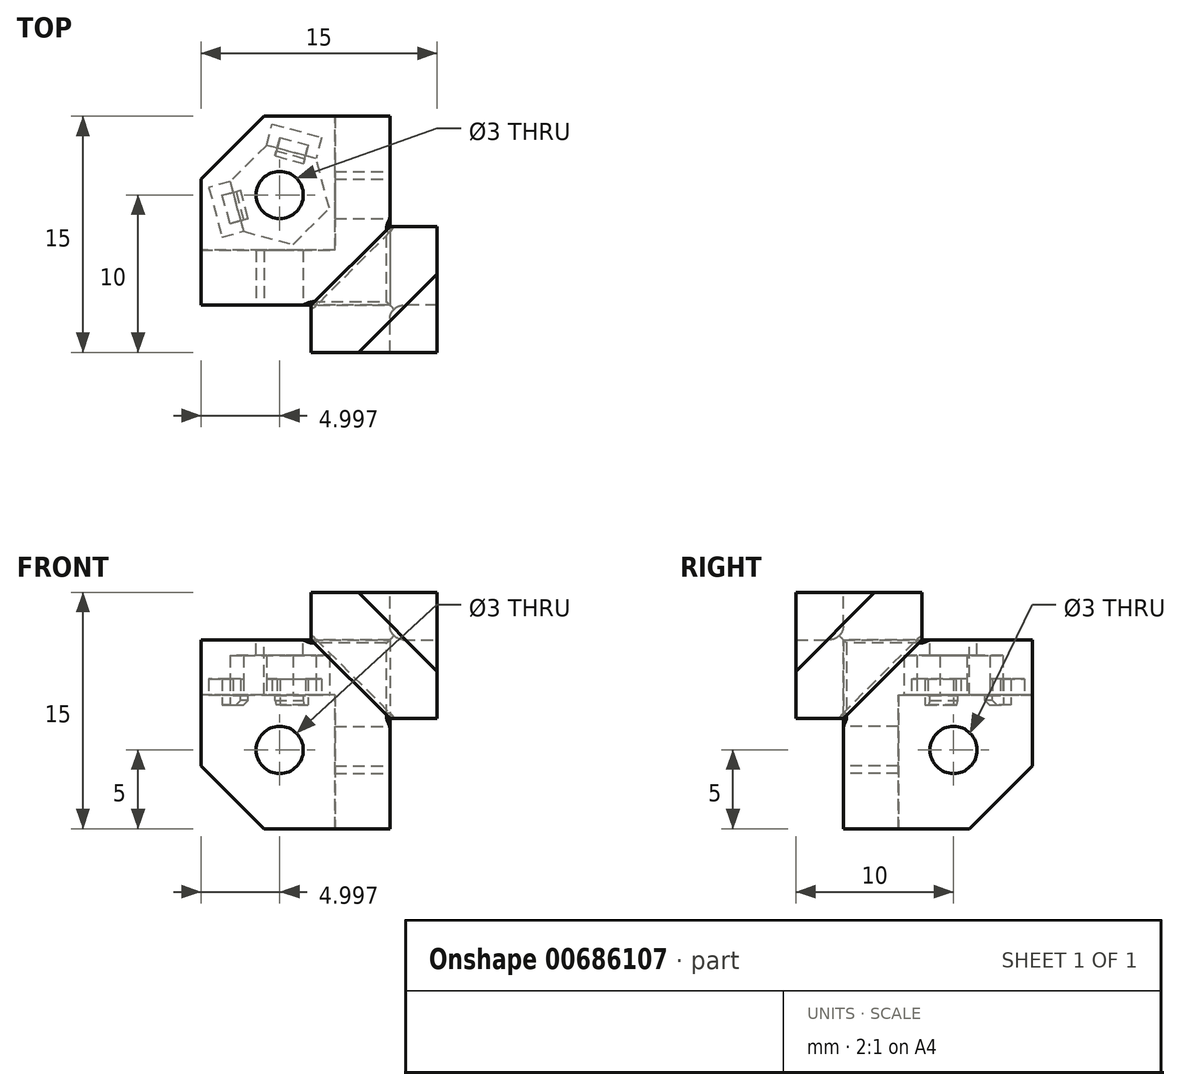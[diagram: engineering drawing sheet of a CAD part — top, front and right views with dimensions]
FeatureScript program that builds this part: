
annotation { "Feature Type Name" : "Feature", "Feature Type Description" : "" }
export const myFeature = defineFeature(function(context is Context, id is Id, definition is map)
    precondition{}
    {
        {
            var Q0;
            Q0=qCreatedBy(makeId("Front.planeOp"),FACE);
            var sketch = newSketch(context, id + "F0", { "sketchPlane" : qUnion([Q0])});
            skLineSegment(sketch, "E0", {"start": v(7.23, 37.22) * mm, "end": v(15.23, 37.22) * mm});
            skLineSegment(sketch, "E1", {"start": v(15.23, 37.22) * mm, "end": v(15.23, 29.22) * mm});
            skLineSegment(sketch, "E2", {"start": v(15.23, 29.22) * mm, "end": v(12.23, 29.22) * mm});
            skLineSegment(sketch, "E3", {"start": v(12.23, 29.22) * mm, "end": v(7.23, 34.22) * mm});
            skLineSegment(sketch, "E4", {"start": v(7.23, 34.22) * mm, "end": v(7.23, 37.22) * mm});
            skLineSegment(sketch, "E5", {"start": v(15.23, 29.22) * mm, "end": v(15.23, 27.22) * mm, "construction": true});
            skLineSegment(sketch, "E6", {"start": v(15.23, 27.22) * mm, "end": v(5.23, 27.22) * mm, "construction": true});
            skCircle(sketch, "E7", {"center": v(5.23, 27.22) * mm, "radius": 1.5 * mm});
            skLineSegment(sketch, "E8", {"start": v(7.23, 37.22) * mm, "end": v(0.23, 37.22) * mm});
            skLineSegment(sketch, "E9", {"start": v(0.23, 37.22) * mm, "end": v(0.23, 26.22) * mm});
            skLineSegment(sketch, "E10", {"start": v(0.23, 26.22) * mm, "end": v(4.23, 22.22) * mm});
            skLineSegment(sketch, "E11", {"start": v(4.23, 22.22) * mm, "end": v(15.23, 22.22) * mm});
            skLineSegment(sketch, "E12", {"start": v(15.23, 22.22) * mm, "end": v(15.23, 29.22) * mm});
            skSolve(sketch);
        }
        {
            var Q0;
            Q0=makeQuery(id+"F0.imprint","IMPRINT",FACE,{"disambiguationData":[TD([[makeQuery(id+"F0.imprint","IMPRINT",EDGE,{"derivedFrom":sQuery(id+"F0.wireOp",EDGE,"E0")}),-1.0]])]});
            extrude(context, id + "F1", {"entities" : qUnion([Q0]), "depth" : 3 * mm, "offsetDistance" : 25 * mm});
        }
        {
            var Q0;
            Q0=makeQuery(id+"F0.imprint","IMPRINT",FACE,{"disambiguationData":[TD([[makeQuery(id+"F0.imprint","IMPRINT",EDGE,{"derivedFrom":sQuery(id+"F0.wireOp",EDGE,"E2")}),1.0]])]});
            var Q1;
            Q1=makeQuery(id+"F0.imprint","IMPRINT",FACE,{"disambiguationData":[TD([[makeQuery(id+"F0.imprint","IMPRINT",EDGE,{"derivedFrom":sQuery(id+"F0.wireOp",EDGE,"E0")}),-1.0]])]});
            extrude(context, id + "F2", {"entities" : qUnion([Q0, Q1]), "operationType" : NewBodyOperationType.ADD, "oppositeDirection" : true, "depth" : 2.5 * mm, "offsetDistance" : 25 * mm});
        }
        {
            var Q0;
            {var subQ0=sQuery(id+"F0.wireOp",EDGE,"E0");Q0=makeQuery(id+"F2.boolean.opBoolean","MERGE",FACE,{"derivedFrom":[makeQuery(id+"F1.opExtrude","SWEPT_FACE",FACE,{"disambiguationData":[OSD([subQ0])]}),makeQuery(id+"F2.opExtrude","SWEPT_FACE",FACE,{"disambiguationData":[OSD([subQ0,sQuery(id+"F0.wireOp",EDGE,"E8")])]})]});}
            var sketch = newSketch(context, id + "F3", { "sketchPlane" : qUnion([Q0])});
            skLineSegment(sketch, "E13", {"start": v(7.23, -3) * mm, "end": v(15.23, -3) * mm});
            skLineSegment(sketch, "E14", {"start": v(15.23, -3) * mm, "end": v(15.23, 5) * mm});
            skLineSegment(sketch, "E15", {"start": v(15.23, 5) * mm, "end": v(12.23, 5) * mm});
            skLineSegment(sketch, "E16", {"start": v(12.23, 5) * mm, "end": v(7.23, 0) * mm});
            skLineSegment(sketch, "E17", {"start": v(12.23, 5) * mm, "end": v(12.23, 12) * mm});
            skLineSegment(sketch, "E18", {"start": v(12.23, 12) * mm, "end": v(4.23, 12) * mm});
            skLineSegment(sketch, "E19", {"start": v(4.23, 12) * mm, "end": v(0.23, 8) * mm});
            skPoint(sketch, "E19.endSnap0", {"position": v(0.23, 1.25) * mm});
            skLineSegment(sketch, "E20", {"start": v(0.23, 8) * mm, "end": v(0.23, 0) * mm});
            skLineSegment(sketch, "E21", {"start": v(8.02, -3) * mm, "end": v(5.23, -3) * mm, "construction": true});
            skLineSegment(sketch, "E22", {"start": v(5.23, -3) * mm, "end": v(5.23, 7) * mm, "construction": true});
            skCircle(sketch, "E23", {"center": v(5.23, 7) * mm, "radius": 1.5 * mm});
            skSolve(sketch);
        }
        {
            var Q0;
            {var subQ1=sQuery(id+"F3.wireOp",EDGE,"E17");Q0=makeQuery(id+"F3.imprint","IMPRINT",FACE,{"disambiguationData":[TD([[makeQuery(id+"F3.imprint","IMPRINT",EDGE,{"derivedFrom":subQ1}),1.0]])]});}
            var Q1;
            {var subQ3=sQuery(id+"F3.wireOp",EDGE,"E15");Q1=makeQuery(id+"F3.imprint","IMPRINT",FACE,{"disambiguationData":[TD([[makeQuery(id+"F3.imprint","IMPRINT",EDGE,{"derivedFrom":subQ3}),1.0]])]});}
            extrude(context, id + "F4", {"entities" : qUnion([Q0, Q1]), "operationType" : NewBodyOperationType.ADD, "oppositeDirection" : true, "depth" : 5.5 * mm, "offsetDistance" : 25 * mm});
        }
        {
            var Q0;
            {var subQ1=sQuery(id+"F3.wireOp",EDGE,"E17");Q0=makeQuery(id+"F3.imprint","IMPRINT",FACE,{"disambiguationData":[TD([[makeQuery(id+"F3.imprint","IMPRINT",EDGE,{"derivedFrom":subQ1}),1.0]])]});}
            var Q1;
            {var subQ1=sQuery(id+"F0.wireOp",EDGE,"E8");var subQ2=sQuery(id+"F0.wireOp",EDGE,"E0");var subQ3=makeQuery(id+"F2.opExtrude","CAP_EDGE",EDGE,{"disambiguationData":[OSD([subQ2,subQ1])],"isStart":true});Q1=makeQuery(id+"F3.imprint","IMPRINT",FACE,{"disambiguationData":[TD([[makeQuery(id+"F3.imprint","IMPRINT",EDGE,{"derivedFrom":subQ3}),-1.0]])]});}
            extrude(context, id + "F5", {"entities" : qUnion([Q0, Q1]), "operationType" : NewBodyOperationType.REMOVE, "oppositeDirection" : true, "depth" : 3 * mm, "offsetDistance" : 25 * mm});
        }
        {
            var Q0;
            {var subQ0=sQuery(id+"F0.wireOp",EDGE,"E1");Q0=makeQuery(id+"F2.boolean.opBoolean","MERGE",FACE,{"derivedFrom":[makeQuery(id+"F1.opExtrude","SWEPT_FACE",FACE,{"disambiguationData":[OSD([subQ0])]}),makeQuery(id+"F2.opExtrude","SWEPT_FACE",FACE,{"disambiguationData":[OSD([subQ0,sQuery(id+"F0.wireOp",EDGE,"E12")])]})]});}
            var sketch = newSketch(context, id + "F6", { "sketchPlane" : qUnion([Q0])});
            skLineSegment(sketch, "E24", {"start": v(0, 29.22) * mm, "end": v(0, 22.22) * mm});
            skLineSegment(sketch, "E25", {"start": v(0, 22.22) * mm, "end": v(8, 22.22) * mm});
            skLineSegment(sketch, "E26", {"start": v(12, 34.22) * mm, "end": v(12, 26.22) * mm});
            skLineSegment(sketch, "E27", {"start": v(12, 26.22) * mm, "end": v(8, 22.22) * mm});
            skLineSegment(sketch, "E28", {"start": v(-3, 29.22) * mm, "end": v(-3, 27.22) * mm, "construction": true});
            skLineSegment(sketch, "E29", {"start": v(-3, 27.22) * mm, "end": v(7, 27.22) * mm, "construction": true});
            skCircle(sketch, "E30", {"center": v(7, 27.22) * mm, "radius": 1.5 * mm});
            skLineSegment(sketch, "E31", {"start": v(12, 34.22) * mm, "end": v(5, 34.22) * mm});
            skLineSegment(sketch, "E32", {"start": v(5, 34.22) * mm, "end": v(0, 29.22) * mm});
            skSolve(sketch);
        }
        {
            var Q0;
            Q0=qSketchRegion(id+"F6",true);
            extrude(context, id + "F7", {"entities" : qUnion([Q0]), "operationType" : NewBodyOperationType.ADD, "oppositeDirection" : true, "depth" : 5.5 * mm, "offsetDistance" : 25 * mm});
        }
        {
            var Q0;
            {var subQ2=sQuery(id+"F6.wireOp",EDGE,"E24");Q0=makeQuery(id+"F6.imprint","IMPRINT",FACE,{"disambiguationData":[TD([[makeQuery(id+"F6.imprint","IMPRINT",EDGE,{"derivedFrom":subQ2}),-1.0]])]});}
            var Q1;
            Q1=makeQuery(id+"F6.imprint","IMPRINT",FACE,{"disambiguationData":[TD([[makeQuery(id+"F6.imprint","IMPRINT",EDGE,{"derivedFrom":sQuery(id+"F6.wireOp",EDGE,"E26")}),-1.0]])]});
            var Q2;
            {var subQ1=sQuery(id+"F3.wireOp",EDGE,"E14");var subQ2=makeQuery(id+"F4.opExtrude","CAP_EDGE",EDGE,{"disambiguationData":[OSD([subQ1])],"isStart":false});Q2=makeQuery(id+"F6.imprint","IMPRINT",FACE,{"disambiguationData":[TD([[makeQuery(id+"F6.imprint","IMPRINT",EDGE,{"derivedFrom":subQ2}),1.0]])]});}
            extrude(context, id + "F8", {"entities" : qUnion([Q0, Q1, Q2]), "operationType" : NewBodyOperationType.REMOVE, "oppositeDirection" : true, "depth" : 3 * mm, "offsetDistance" : 25 * mm});
        }
        {
            var Q0;
            Q0=makeQuery(id+"F1.opExtrude","CAP_FACE",FACE,{"disambiguationData":[OSD([sQuery(id+"F0.wireOp",EDGE,"E0"),sQuery(id+"F0.wireOp",EDGE,"E1"),sQuery(id+"F0.wireOp",EDGE,"E2"),sQuery(id+"F0.wireOp",EDGE,"E3"),sQuery(id+"F0.wireOp",EDGE,"E4")])],"isStart":false});
            var sketch = newSketch(context, id + "F9", { "sketchPlane" : qUnion([Q0])});
            skLineSegment(sketch, "E33", {"start": v(15.23, 37.22) * mm, "end": v(15.23, 32.22) * mm});
            skLineSegment(sketch, "E34", {"start": v(15.23, 32.22) * mm, "end": v(10.23, 37.22) * mm});
            skLineSegment(sketch, "E35", {"start": v(10.23, 37.22) * mm, "end": v(15.23, 37.22) * mm});
            skSolve(sketch);
        }
        {
            var Q0;
            Q0=makeQuery(id+"F9.imprint","IMPRINT",FACE,{"disambiguationData":[TD([[makeQuery(id+"F9.imprint","IMPRINT",EDGE,{"derivedFrom":sQuery(id+"F9.wireOp",EDGE,"E33")}),-1.0]])]});
            extrude(context, id + "F10", {"entities" : qUnion([Q0]), "operationType" : NewBodyOperationType.REMOVE, "oppositeDirection" : true, "depth" : 5 * mm, "offsetDistance" : 25 * mm});
        }
        {
            var Q0;
            Q0=makeQuery(id+"F10.boolean.opBoolean","COPY",EDGE,{"derivedFrom":makeQuery(id+"F10.opExtrude","CAP_EDGE",EDGE,{"disambiguationData":[OSD([sQuery(id+"F9.wireOp",EDGE,"E34")])],"isStart":false})});
            chamfer(context, id + "F11", {"entities" : qUnion([Q0]), "chamferType" : ChamferType.OFFSET_ANGLE, "width" : 5 * mm, "oppositeDirection" : false, "angle" : 35.4 * degree, "tangentPropagation" : true});
        }
        {
            var Q0;
            {var subQ0=sQuery(id+"F0.wireOp",EDGE,"E2");Q0=makeQuery(id+"F8.boolean.opBoolean","MERGE",VERTEX,{"derivedFrom":[makeQuery(id+"F1.opExtrude","CAP_VERTEX",VERTEX,{"disambiguationData":[OSD([subQ0,sQuery(id+"F0.wireOp",EDGE,"E3")])],"isStart":true}),makeQuery(id+"F8.opExtrude","CAP_VERTEX",VERTEX,{"disambiguationData":[OSD([sQuery(id+"F0.wireOp",EDGE,"E1"),subQ0,sQuery(id+"F0.wireOp",EDGE,"E12"),sQuery(id+"F6.wireOp",EDGE,"E24"),sQuery(id+"F6.wireOp",EDGE,"E32")])],"isStart":false})]});}
            var Q1;
            {var subQ0=sQuery(id+"F0.wireOp",EDGE,"E4");Q1=makeQuery(id+"F5.boolean.opBoolean","MERGE",VERTEX,{"derivedFrom":[makeQuery(id+"F1.opExtrude","CAP_VERTEX",VERTEX,{"disambiguationData":[OSD([sQuery(id+"F0.wireOp",EDGE,"E3"),subQ0])],"isStart":true}),makeQuery(id+"F5.opExtrude","CAP_VERTEX",VERTEX,{"disambiguationData":[OSD([sQuery(id+"F0.wireOp",EDGE,"E0"),subQ0,sQuery(id+"F0.wireOp",EDGE,"E8"),sQuery(id+"F3.wireOp",EDGE,"E16")])],"isStart":false})]});}
            var Q2;
            {var subQ0=sQuery(id+"F3.wireOp",EDGE,"E15");Q2=makeQuery(id+"F8.boolean.opBoolean","MERGE",VERTEX,{"derivedFrom":[makeQuery(id+"F5.boolean.opBoolean","COPY",VERTEX,{"derivedFrom":makeQuery(id+"F5.opExtrude","CAP_VERTEX",VERTEX,{"disambiguationData":[OSD([subQ0,sQuery(id+"F3.wireOp",EDGE,"E16"),sQuery(id+"F3.wireOp",EDGE,"E17")])],"isStart":false})}),makeQuery(id+"F8.opExtrude","CAP_VERTEX",VERTEX,{"disambiguationData":[OSD([sQuery(id+"F3.wireOp",EDGE,"E14"),subQ0,sQuery(id+"F6.wireOp",EDGE,"E31"),sQuery(id+"F6.wireOp",EDGE,"E32")])],"isStart":false})]});}
            cPlane(context, id + "F12", {"entities" : qUnion([Q0, Q1, Q2]), "cplaneType" : CPlaneType.THREE_POINT, "offset" : 25 * mm, "width" : 150 * mm, "height" : 150 * mm});
        }
        {
            var Q0;
            Q0=qCreatedBy(id+"F12.planeOp",FACE);
            var sketch = newSketch(context, id + "F13", { "sketchPlane" : qUnion([Q0])});
            skLineSegment(sketch, "E36", {"start": v(-8.07, 24.2) * mm, "end": v(-1.95, 20.66) * mm});
            skLineSegment(sketch, "E37", {"start": v(-1.95, 27.73) * mm, "end": v(-8.07, 24.2) * mm});
            skLineSegment(sketch, "E38", {"start": v(-1.95, 20.66) * mm, "end": v(-1.95, 27.73) * mm});
            skLineSegment(sketch, "E39.0", {"start": v(-2.15, 27.39) * mm, "end": v(-7.67, 24.2) * mm});
            skLineSegment(sketch, "E39.1", {"start": v(-2.15, 21) * mm, "end": v(-2.15, 27.39) * mm});
            skLineSegment(sketch, "E39.2", {"start": v(-7.67, 24.2) * mm, "end": v(-2.15, 21) * mm});
            skLineSegment(sketch, "E40.0", {"start": v(-1.07, 29.26) * mm, "end": v(-9.83, 24.2) * mm});
            skLineSegment(sketch, "E40.1", {"start": v(-1.07, 19.14) * mm, "end": v(-1.07, 29.26) * mm});
            skLineSegment(sketch, "E40.2", {"start": v(-9.83, 24.2) * mm, "end": v(-1.07, 19.14) * mm});
            skSolve(sketch);
        }
        {
            var Q0;
            Q0=qSketchRegion(id+"F13",true);
            var Q1;
            Q1=makeQuery(id+"F13.imprint","IMPRINT",FACE,{"disambiguationData":[TD([[makeQuery(id+"F13.imprint","IMPRINT",EDGE,{"derivedFrom":sQuery(id+"F13.wireOp",EDGE,"E36")}),1.0]])]});
            extrude(context, id + "F14", {"entities" : qUnion([Q0, Q1]), "operationType" : NewBodyOperationType.REMOVE, "endBound" : BoundingType.SYMMETRIC, "depth" : .6 * mm, "offsetDistance" : 25 * mm});
        }
        {
            var Q0;
            Q0=makeQuery(id+"F14.boolean.opBoolean","COPY",EDGE,{"derivedFrom":makeQuery(id+"F14.opExtrude","CAP_EDGE",EDGE,{"disambiguationData":[OSD([sQuery(id+"F13.wireOp",EDGE,"E39.0")])],"isStart":true})});
            var Q1;
            Q1=makeQuery(id+"F14.boolean.opBoolean","COPY",EDGE,{"derivedFrom":makeQuery(id+"F14.opExtrude","CAP_EDGE",EDGE,{"disambiguationData":[OSD([sQuery(id+"F13.wireOp",EDGE,"E39.1")])],"isStart":true})});
            var Q2;
            Q2=makeQuery(id+"F14.boolean.opBoolean","COPY",EDGE,{"derivedFrom":makeQuery(id+"F14.opExtrude","CAP_EDGE",EDGE,{"disambiguationData":[OSD([sQuery(id+"F13.wireOp",EDGE,"E39.0")])],"isStart":false})});
            var Q3;
            Q3=makeQuery(id+"F14.boolean.opBoolean","COPY",EDGE,{"derivedFrom":makeQuery(id+"F14.opExtrude","CAP_EDGE",EDGE,{"disambiguationData":[OSD([sQuery(id+"F13.wireOp",EDGE,"E39.1")])],"isStart":false})});
            var Q4;
            Q4=makeQuery(id+"F14.boolean.opBoolean","COPY",EDGE,{"derivedFrom":makeQuery(id+"F14.opExtrude","CAP_EDGE",EDGE,{"disambiguationData":[OSD([sQuery(id+"F13.wireOp",EDGE,"E39.2")])],"isStart":true})});
            var Q5;
            Q5=makeQuery(id+"F14.boolean.opBoolean","COPY",EDGE,{"derivedFrom":makeQuery(id+"F14.opExtrude","CAP_EDGE",EDGE,{"disambiguationData":[OSD([sQuery(id+"F13.wireOp",EDGE,"E39.2")])],"isStart":false})});
            fillet(context, id + "F15", {"entities" : qUnion([Q0, Q1, Q2, Q3, Q4, Q5]), "radius" : .3 * mm, "tangentPropagation" : true, "allowEdgeOverflow" : false});
        }
        {
            var Q0;
            Q0=makeQuery(id+"F14.boolean.opBoolean","INTERSECT",EDGE,{"derivedFrom":[makeQuery(id+"F8.boolean.opBoolean","COPY",FACE,{"derivedFrom":makeQuery(id+"F8.opExtrude","SWEPT_FACE",FACE,{"disambiguationData":[OSD([sQuery(id+"F6.wireOp",EDGE,"E32")])]})}),makeQuery(id+"F14.opExtrude","CAP_FACE",FACE,{"disambiguationData":[OSD([sQuery(id+"F13.wireOp",EDGE,"E39.0"),sQuery(id+"F13.wireOp",EDGE,"E39.1"),sQuery(id+"F13.wireOp",EDGE,"E39.2"),sQuery(id+"F13.wireOp",EDGE,"E40.0"),sQuery(id+"F13.wireOp",EDGE,"E40.1"),sQuery(id+"F13.wireOp",EDGE,"E40.2")])],"isStart":false})]});
            var Q1;
            Q1=makeQuery(id+"F14.boolean.opBoolean","INTERSECT",EDGE,{"derivedFrom":[makeQuery(id+"F1.opExtrude","SWEPT_FACE",FACE,{"disambiguationData":[OSD([sQuery(id+"F0.wireOp",EDGE,"E3")])]}),makeQuery(id+"F14.opExtrude","CAP_FACE",FACE,{"disambiguationData":[OSD([sQuery(id+"F13.wireOp",EDGE,"E39.0"),sQuery(id+"F13.wireOp",EDGE,"E39.1"),sQuery(id+"F13.wireOp",EDGE,"E39.2"),sQuery(id+"F13.wireOp",EDGE,"E40.0"),sQuery(id+"F13.wireOp",EDGE,"E40.1"),sQuery(id+"F13.wireOp",EDGE,"E40.2")])],"isStart":false})]});
            var Q2;
            Q2=makeQuery(id+"F14.boolean.opBoolean","INTERSECT",EDGE,{"derivedFrom":[makeQuery(id+"F5.boolean.opBoolean","COPY",FACE,{"derivedFrom":makeQuery(id+"F5.opExtrude","SWEPT_FACE",FACE,{"disambiguationData":[OSD([sQuery(id+"F3.wireOp",EDGE,"E16")])]})}),makeQuery(id+"F14.opExtrude","CAP_FACE",FACE,{"disambiguationData":[OSD([sQuery(id+"F13.wireOp",EDGE,"E39.0"),sQuery(id+"F13.wireOp",EDGE,"E39.1"),sQuery(id+"F13.wireOp",EDGE,"E39.2"),sQuery(id+"F13.wireOp",EDGE,"E40.0"),sQuery(id+"F13.wireOp",EDGE,"E40.1"),sQuery(id+"F13.wireOp",EDGE,"E40.2")])],"isStart":false})]});
            fillet(context, id + "F16", {"entities" : qUnion([Q0, Q1, Q2]), "radius" : 1 * mm, "tangentPropagation" : true, "allowEdgeOverflow" : false});
        }
        {
            var Q0;
            Q0=makeQuery(id+"F14.boolean.opBoolean","INTERSECT",EDGE,{"derivedFrom":[makeQuery(id+"F2.opExtrude","CAP_FACE",FACE,{"disambiguationData":[OSD([sQuery(id+"F0.wireOp",EDGE,"E0"),sQuery(id+"F0.wireOp",EDGE,"E1"),sQuery(id+"F0.wireOp",EDGE,"E7"),sQuery(id+"F0.wireOp",EDGE,"E8"),sQuery(id+"F0.wireOp",EDGE,"E9"),sQuery(id+"F0.wireOp",EDGE,"E10"),sQuery(id+"F0.wireOp",EDGE,"E11"),sQuery(id+"F0.wireOp",EDGE,"E12")])],"isStart":true}),makeQuery(id+"F14.opExtrude","CAP_FACE",FACE,{"disambiguationData":[OSD([sQuery(id+"F13.wireOp",EDGE,"E39.0"),sQuery(id+"F13.wireOp",EDGE,"E39.1"),sQuery(id+"F13.wireOp",EDGE,"E39.2"),sQuery(id+"F13.wireOp",EDGE,"E40.0"),sQuery(id+"F13.wireOp",EDGE,"E40.1"),sQuery(id+"F13.wireOp",EDGE,"E40.2")])],"isStart":true})]});
            var Q1;
            Q1=makeQuery(id+"F14.boolean.opBoolean","INTERSECT",EDGE,{"derivedFrom":[makeQuery(id+"F8.boolean.opBoolean","COPY",FACE,{"derivedFrom":makeQuery(id+"F8.opExtrude","CAP_FACE",FACE,{"disambiguationData":[OSD([sQuery(id+"F6.wireOp",EDGE,"E24"),sQuery(id+"F6.wireOp",EDGE,"E25"),sQuery(id+"F6.wireOp",EDGE,"E26"),sQuery(id+"F6.wireOp",EDGE,"E27"),sQuery(id+"F6.wireOp",EDGE,"E30"),sQuery(id+"F6.wireOp",EDGE,"E31"),sQuery(id+"F6.wireOp",EDGE,"E32")])],"isStart":false})}),makeQuery(id+"F14.opExtrude","CAP_FACE",FACE,{"disambiguationData":[OSD([sQuery(id+"F13.wireOp",EDGE,"E39.0"),sQuery(id+"F13.wireOp",EDGE,"E39.1"),sQuery(id+"F13.wireOp",EDGE,"E39.2"),sQuery(id+"F13.wireOp",EDGE,"E40.0"),sQuery(id+"F13.wireOp",EDGE,"E40.1"),sQuery(id+"F13.wireOp",EDGE,"E40.2")])],"isStart":true})]});
            var Q2;
            Q2=makeQuery(id+"F14.boolean.opBoolean","INTERSECT",EDGE,{"derivedFrom":[makeQuery(id+"F7.boolean.opBoolean","MERGE",FACE,{"derivedFrom":[makeQuery(id+"F5.boolean.opBoolean","COPY",FACE,{"derivedFrom":makeQuery(id+"F5.opExtrude","CAP_FACE",FACE,{"disambiguationData":[OSD([sQuery(id+"F0.wireOp",EDGE,"E0"),sQuery(id+"F0.wireOp",EDGE,"E8"),sQuery(id+"F3.wireOp",EDGE,"E16"),sQuery(id+"F3.wireOp",EDGE,"E17"),sQuery(id+"F3.wireOp",EDGE,"E18"),sQuery(id+"F3.wireOp",EDGE,"E19"),sQuery(id+"F3.wireOp",EDGE,"E20"),sQuery(id+"F3.wireOp",EDGE,"E23")])],"isStart":false})}),makeQuery(id+"F7.opExtrude","SWEPT_FACE",FACE,{"disambiguationData":[OSD([sQuery(id+"F6.wireOp",EDGE,"E31")])]})]}),makeQuery(id+"F14.opExtrude","CAP_FACE",FACE,{"disambiguationData":[OSD([sQuery(id+"F13.wireOp",EDGE,"E39.0"),sQuery(id+"F13.wireOp",EDGE,"E39.1"),sQuery(id+"F13.wireOp",EDGE,"E39.2"),sQuery(id+"F13.wireOp",EDGE,"E40.0"),sQuery(id+"F13.wireOp",EDGE,"E40.1"),sQuery(id+"F13.wireOp",EDGE,"E40.2")])],"isStart":true})]});
            fillet(context, id + "F17", {"entities" : qUnion([Q0, Q1, Q2]), "radius" : .2 * mm, "tangentPropagation" : true, "allowEdgeOverflow" : false});
        }
        {
            var Q0;
            Q0=makeQuery(id+"F2.opExtrude","CAP_FACE",FACE,{"disambiguationData":[OSD([sQuery(id+"F0.wireOp",EDGE,"E0"),sQuery(id+"F0.wireOp",EDGE,"E1"),sQuery(id+"F0.wireOp",EDGE,"E7"),sQuery(id+"F0.wireOp",EDGE,"E8"),sQuery(id+"F0.wireOp",EDGE,"E9"),sQuery(id+"F0.wireOp",EDGE,"E10"),sQuery(id+"F0.wireOp",EDGE,"E11"),sQuery(id+"F0.wireOp",EDGE,"E12")])],"isStart":false});
            extrude(context, id + "F18", {"entities" : qUnion([Q0]), "operationType" : NewBodyOperationType.ADD, "depth" : 1 * mm, "offsetDistance" : 25 * mm});
        }
        {
            var Q0;
            Q0=makeQuery(id+"F7.opExtrude","CAP_FACE",FACE,{"disambiguationData":[OSD([sQuery(id+"F6.wireOp",EDGE,"E24"),sQuery(id+"F6.wireOp",EDGE,"E25"),sQuery(id+"F6.wireOp",EDGE,"E26"),sQuery(id+"F6.wireOp",EDGE,"E27"),sQuery(id+"F6.wireOp",EDGE,"E30"),sQuery(id+"F6.wireOp",EDGE,"E31"),sQuery(id+"F6.wireOp",EDGE,"E32")])],"isStart":false});
            extrude(context, id + "F19", {"entities" : qUnion([Q0]), "operationType" : NewBodyOperationType.ADD, "depth" : 1 * mm, "offsetDistance" : 25 * mm});
        }
        {
            var Q0;
            Q0=makeQuery(id+"F4.opExtrude","CAP_FACE",FACE,{"disambiguationData":[OSD([sQuery(id+"F0.wireOp",EDGE,"E0"),sQuery(id+"F0.wireOp",EDGE,"E8"),sQuery(id+"F3.wireOp",EDGE,"E14"),sQuery(id+"F3.wireOp",EDGE,"E15"),sQuery(id+"F3.wireOp",EDGE,"E17"),sQuery(id+"F3.wireOp",EDGE,"E18"),sQuery(id+"F3.wireOp",EDGE,"E19"),sQuery(id+"F3.wireOp",EDGE,"E20"),sQuery(id+"F3.wireOp",EDGE,"E23")])],"isStart":false});
            extrude(context, id + "F20", {"entities" : qUnion([Q0]), "operationType" : NewBodyOperationType.ADD, "depth" : 1 * mm, "offsetDistance" : 25 * mm});
        }
        {
            var Q0;
            Q0=makeQuery(id+"F20.opExtrude","CAP_FACE",FACE,{"disambiguationData":[OSD([sQuery(id+"F0.wireOp",EDGE,"E0"),sQuery(id+"F0.wireOp",EDGE,"E8"),sQuery(id+"F3.wireOp",EDGE,"E14"),sQuery(id+"F3.wireOp",EDGE,"E15"),sQuery(id+"F3.wireOp",EDGE,"E17"),sQuery(id+"F3.wireOp",EDGE,"E18"),sQuery(id+"F3.wireOp",EDGE,"E19"),sQuery(id+"F3.wireOp",EDGE,"E20"),sQuery(id+"F3.wireOp",EDGE,"E23")])],"isStart":false});
            var sketch = newSketch(context, id + "F21", { "sketchPlane" : qUnion([Q0])});
            skCircle(sketch, "E41.cCircle", {"center": v(5.23, -7) * mm, "radius": 2.83 * mm, "construction": true});
            skLineSegment(sketch, "E41.0", {"start": v(4.38, -10.15) * mm, "end": v(2.08, -7.84) * mm});
            skLineSegment(sketch, "E41.1", {"start": v(2.08, -7.84) * mm, "end": v(2.92, -4.7) * mm});
            skLineSegment(sketch, "E41.2", {"start": v(2.92, -4.7) * mm, "end": v(6.07, -3.85) * mm});
            skLineSegment(sketch, "E41.3", {"start": v(6.07, -3.85) * mm, "end": v(8.38, -6.16) * mm});
            skLineSegment(sketch, "E41.4", {"start": v(8.38, -6.16) * mm, "end": v(7.53, -9.3) * mm});
            skLineSegment(sketch, "E41.5", {"start": v(7.53, -9.3) * mm, "end": v(4.38, -10.15) * mm});
            skPoint(sketch, "E41.0.midPoint", {"position": v(3.23, -9) * mm});
            skLineSegment(sketch, "E42", {"start": v(2.74, -5.37) * mm, "end": v(2.06, -5.19) * mm});
            skLineSegment(sketch, "E43", {"start": v(2.06, -5.19) * mm, "end": v(1.58, -6.99) * mm});
            skLineSegment(sketch, "E44", {"start": v(1.58, -6.99) * mm, "end": v(2.26, -7.17) * mm});
            skLineSegment(sketch, "E45", {"start": v(2.08, -7.84) * mm, "end": v(0.72, -7.48) * mm});
            skLineSegment(sketch, "E46", {"start": v(0.72, -7.48) * mm, "end": v(1.57, -4.33) * mm});
            skLineSegment(sketch, "E47", {"start": v(1.57, -4.33) * mm, "end": v(2.92, -4.7) * mm});
            skLineSegment(sketch, "E48", {"start": v(2.26, -7.17) * mm, "end": v(2.55, -7.25) * mm});
            skLineSegment(sketch, "E49", {"start": v(2.55, -7.25) * mm, "end": v(3.03, -5.45) * mm});
            skLineSegment(sketch, "E50", {"start": v(3.03, -5.45) * mm, "end": v(2.74, -5.37) * mm});
            skLineSegment(sketch, "E51", {"start": v(4.38, -10.15) * mm, "end": v(4.75, -11.5) * mm});
            skLineSegment(sketch, "E52", {"start": v(4.75, -11.5) * mm, "end": v(7.9, -10.66) * mm});
            skLineSegment(sketch, "E53", {"start": v(7.9, -10.66) * mm, "end": v(7.53, -9.3) * mm});
            skLineSegment(sketch, "E54", {"start": v(5.06, -9.97) * mm, "end": v(5.24, -10.65) * mm});
            skLineSegment(sketch, "E55", {"start": v(5.24, -10.65) * mm, "end": v(7.04, -10.16) * mm});
            skLineSegment(sketch, "E56", {"start": v(7.04, -10.16) * mm, "end": v(6.86, -9.49) * mm});
            skLineSegment(sketch, "E57", {"start": v(5.06, -9.97) * mm, "end": v(4.98, -9.68) * mm});
            skLineSegment(sketch, "E58", {"start": v(4.98, -9.68) * mm, "end": v(6.78, -9.2) * mm});
            skLineSegment(sketch, "E59", {"start": v(6.78, -9.2) * mm, "end": v(6.86, -9.49) * mm});
            skSolve(sketch);
        }
        {
            var Q0;
            {var subQ1=sQuery(id+"F21.wireOp",EDGE,"E41.0");Q0=makeQuery(id+"F21.imprint","IMPRINT",FACE,{"disambiguationData":[TD([[makeQuery(id+"F21.imprint","IMPRINT",EDGE,{"derivedFrom":subQ1}),-1.0]])]});}
            var Q1;
            {var subQ2=sQuery(id+"F21.wireOp",EDGE,"E48");Q1=makeQuery(id+"F21.imprint","IMPRINT",FACE,{"disambiguationData":[TD([[makeQuery(id+"F21.imprint","IMPRINT",EDGE,{"derivedFrom":subQ2}),1.0]])]});}
            var Q2;
            {var subQ0=sQuery(id+"F21.wireOp",EDGE,"E57");Q2=makeQuery(id+"F21.imprint","IMPRINT",FACE,{"disambiguationData":[TD([[makeQuery(id+"F21.imprint","IMPRINT",EDGE,{"derivedFrom":subQ0}),-1.0]])]});}
            extrude(context, id + "F22", {"entities" : qUnion([Q0, Q1, Q2]), "operationType" : NewBodyOperationType.REMOVE, "oppositeDirection" : true, "depth" : 2.5 * mm, "offsetDistance" : 25 * mm});
        }
        {
            var Q0;
            {var subQ0=sQuery(id+"F21.wireOp",EDGE,"E42");Q0=makeQuery(id+"F21.imprint","IMPRINT",FACE,{"disambiguationData":[TD([[makeQuery(id+"F21.imprint","IMPRINT",EDGE,{"derivedFrom":subQ0}),-1.0]])]});}
            var Q1;
            {var subQ0=sQuery(id+"F21.wireOp",EDGE,"E51");Q1=makeQuery(id+"F21.imprint","IMPRINT",FACE,{"disambiguationData":[TD([[makeQuery(id+"F21.imprint","IMPRINT",EDGE,{"derivedFrom":subQ0}),1.0]])]});}
            extrude(context, id + "F23", {"entities" : qUnion([Q0, Q1]), "operationType" : NewBodyOperationType.REMOVE, "oppositeDirection" : true, "depth" : 1 * mm, "offsetDistance" : 25 * mm});
        }
        {
            var Q0;
            {var subQ0=sQuery(id+"F21.wireOp",EDGE,"E42");Q0=makeQuery(id+"F21.imprint","IMPRINT",FACE,{"disambiguationData":[TD([[makeQuery(id+"F21.imprint","IMPRINT",EDGE,{"derivedFrom":subQ0}),1.0]])]});}
            var Q1;
            {var subQ0=sQuery(id+"F21.wireOp",EDGE,"E54");Q1=makeQuery(id+"F21.imprint","IMPRINT",FACE,{"disambiguationData":[TD([[makeQuery(id+"F21.imprint","IMPRINT",EDGE,{"derivedFrom":subQ0}),1.0]])]});}
            extrude(context, id + "F24", {"entities" : qUnion([Q0, Q1]), "operationType" : NewBodyOperationType.ADD, "endBound" : BoundingType.SYMMETRIC, "depth" : .1 * mm, "offsetDistance" : 25 * mm});
        }
        {
            var Q0;
            Q0=makeQuery(id+"F24.opExtrude","CAP_FACE",FACE,{"disambiguationData":[OSD([sQuery(id+"F21.wireOp",EDGE,"E41.1"),sQuery(id+"F21.wireOp",EDGE,"E42"),sQuery(id+"F21.wireOp",EDGE,"E43"),sQuery(id+"F21.wireOp",EDGE,"E44")])],"isStart":false});
            var sketch = newSketch(context, id + "F25", { "sketchPlane" : qUnion([Q0])});
            skLineSegment(sketch, "E60", {"start": v(2.26, -7.17) * mm, "end": v(2.74, -7.3) * mm});
            skLineSegment(sketch, "E61", {"start": v(2.74, -5.37) * mm, "end": v(3.22, -5.5) * mm});
            skLineSegment(sketch, "E62", {"start": v(3.22, -5.5) * mm, "end": v(2.74, -7.3) * mm});
            skLineSegment(sketch, "E63.0.0", {"start": v(5.24, -10.65) * mm, "end": v(7.04, -10.16) * mm});
            skLineSegment(sketch, "E63.0.1", {"start": v(7.04, -10.16) * mm, "end": v(6.86, -9.49) * mm});
            skLineSegment(sketch, "E63.0.2", {"start": v(6.86, -9.49) * mm, "end": v(5.06, -9.97) * mm});
            skLineSegment(sketch, "E63.0.3", {"start": v(5.06, -9.97) * mm, "end": v(5.24, -10.65) * mm});
            skLineSegment(sketch, "E64", {"start": v(5.06, -9.97) * mm, "end": v(4.93, -9.49) * mm});
            skLineSegment(sketch, "E65", {"start": v(4.93, -9.49) * mm, "end": v(6.73, -9) * mm});
            skLineSegment(sketch, "E66", {"start": v(6.73, -9) * mm, "end": v(6.86, -9.49) * mm});
            skSolve(sketch);
        }
        {
            var Q0;
            Q0=makeQuery(id+"F25.imprint","IMPRINT",FACE,{"disambiguationData":[TD([[makeQuery(id+"F25.imprint","IMPRINT",EDGE,{"derivedFrom":sQuery(id+"F25.wireOp",EDGE,"E60")}),1.0]])]});
            var Q1;
            Q1=makeQuery(id+"F25.imprint","IMPRINT",FACE,{"disambiguationData":[TD([[makeQuery(id+"F25.imprint","IMPRINT",EDGE,{"derivedFrom":makeQuery(id+"F24.opExtrude","CAP_EDGE",EDGE,{"disambiguationData":[OSD([sQuery(id+"F21.wireOp",EDGE,"E41.1")])],"isStart":false})}),1.0]])]});
            var Q2;
            Q2=makeQuery(id+"F25.imprint","IMPRINT",FACE,{"disambiguationData":[TD([[makeQuery(id+"F25.imprint","IMPRINT",EDGE,{"derivedFrom":sQuery(id+"F25.wireOp",EDGE,"E63.0.2")}),-1.0]])]});
            var Q3;
            Q3=makeQuery(id+"F25.imprint","IMPRINT",FACE,{"disambiguationData":[TD([[makeQuery(id+"F25.imprint","IMPRINT",EDGE,{"derivedFrom":sQuery(id+"F25.wireOp",EDGE,"E63.0.0")}),1.0]])]});
            extrude(context, id + "F26", {"entities" : qUnion([Q0, Q1, Q2, Q3]), "operationType" : NewBodyOperationType.ADD, "depth" : .6 * mm, "offsetDistance" : 25 * mm});
        }
        {
            var Q0;
            Q0=makeQuery(id+"F26.opExtrude","CAP_EDGE",EDGE,{"disambiguationData":[OSD([sQuery(id+"F25.wireOp",EDGE,"E62")])],"isStart":false});
            var Q1;
            Q1=makeQuery(id+"F26.opExtrude","CAP_EDGE",EDGE,{"disambiguationData":[OSD([sQuery(id+"F25.wireOp",EDGE,"E65")])],"isStart":false});
            chamfer(context, id + "F27", {"entities" : qUnion([Q0, Q1]), "width" : .3 * mm, "tangentPropagation" : true});
        }
    });
